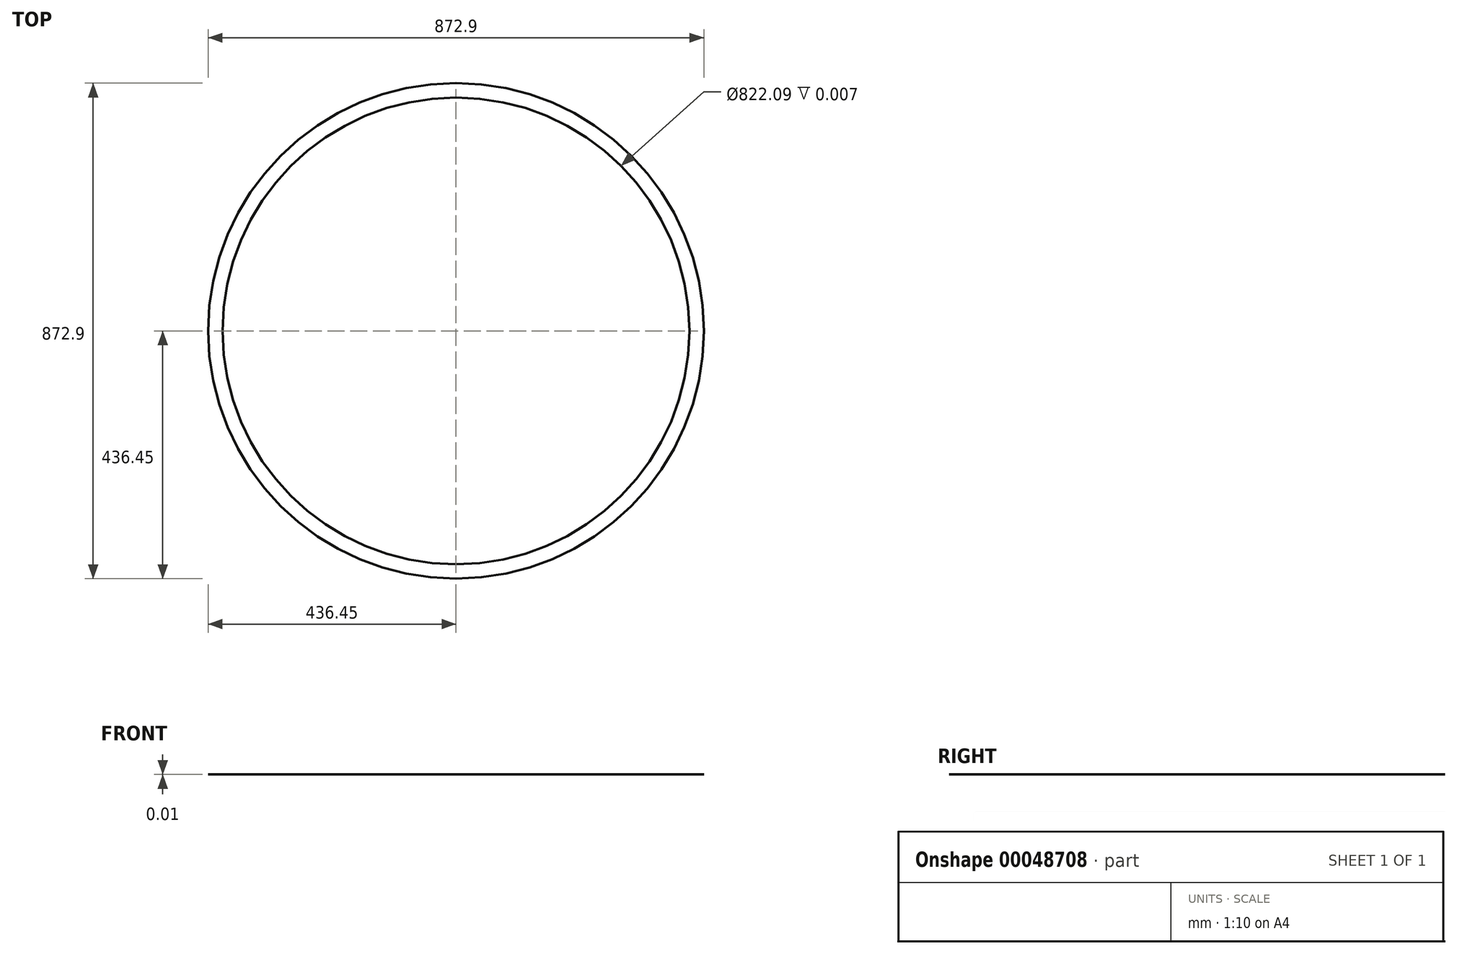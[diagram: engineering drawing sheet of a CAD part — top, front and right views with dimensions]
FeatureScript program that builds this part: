
annotation { "Feature Type Name" : "Feature", "Feature Type Description" : "" }
export const myFeature = defineFeature(function(context is Context, id is Id, definition is map)
    precondition{}
    {
        {
            var Q0;
            Q0=qCreatedBy(makeId("Top.planeOp"),FACE);
            var sketch = newSketch(context, id + "F0", { "sketchPlane" : qUnion([Q0])});
            skCircle(sketch, "E0", {"center": v(0, 0) * mm, "radius": 436.45 * mm});
            skCircle(sketch, "E1", {"center": v(0, 0) * mm, "radius": 411.05 * mm});
            skSolve(sketch);
        }
        {
            var Q0;
            Q0 = qSketchRegion(id + "F0", true);
            extrude(context, id + "F1", {"entities" : qUnion([Q0]), "depth" : 3 / 457.2 * mm});
        }
    });
